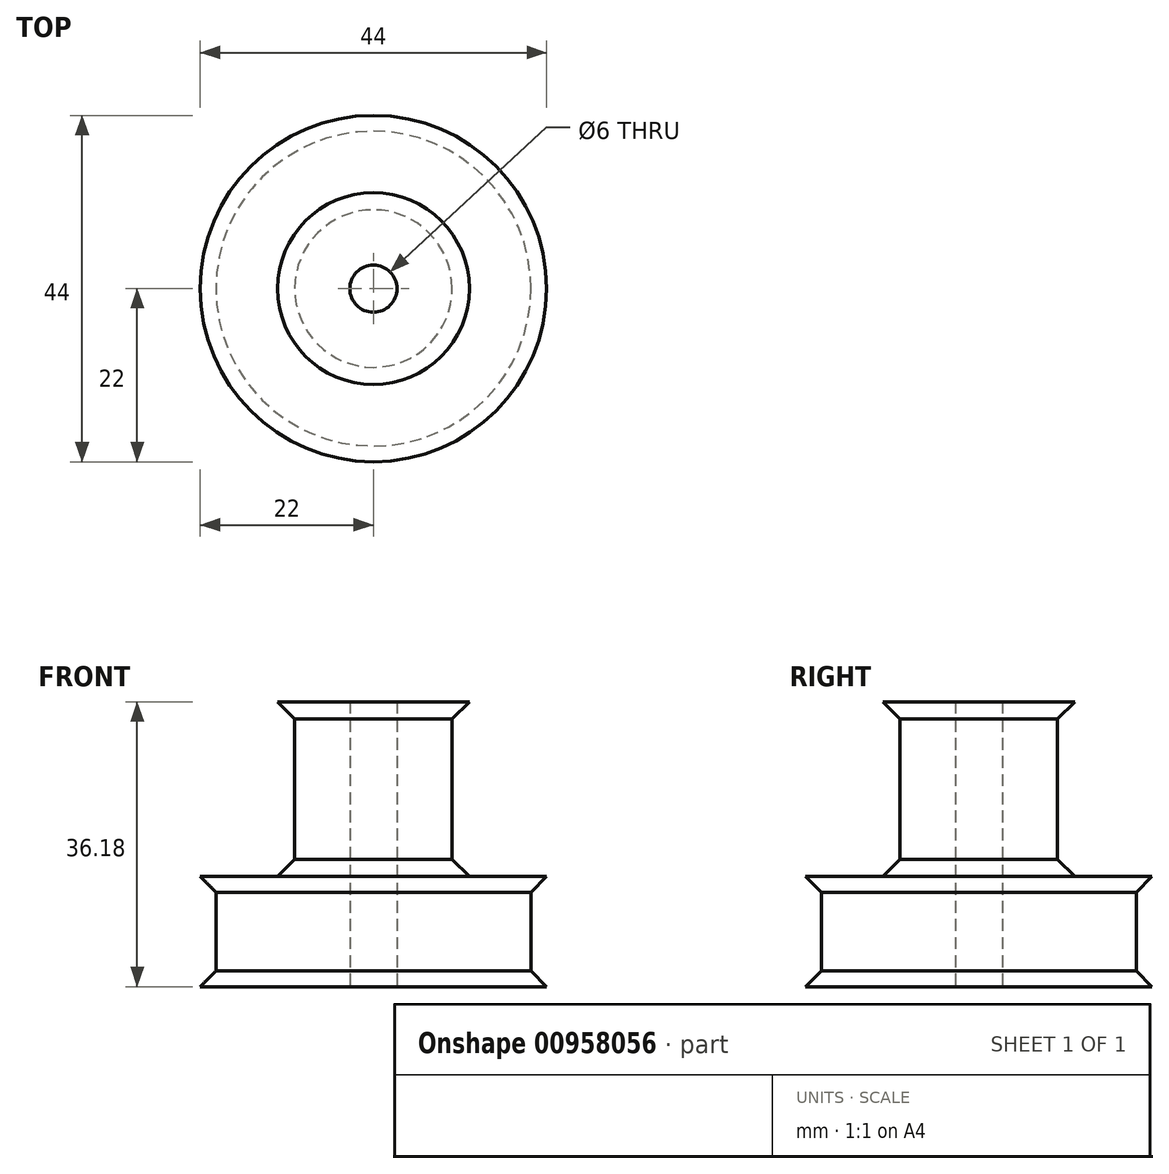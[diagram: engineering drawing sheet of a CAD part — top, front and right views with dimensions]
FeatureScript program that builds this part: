
annotation { "Feature Type Name" : "Feature", "Feature Type Description" : "" }
export const myFeature = defineFeature(function(context is Context, id is Id, definition is map)
    precondition{}
    {
        {
            var Q0;
            Q0=qCreatedBy(makeId("Front.planeOp"),FACE);
            var sketch = newSketch(context, id + "F0", { "sketchPlane" : qUnion([Q0])});
            skLineSegment(sketch, "E0", {"start": v(12.18, 36.18) * mm, "end": v(10, 34) * mm});
            skLineSegment(sketch, "E1", {"start": v(10, 34) * mm, "end": v(10, 16.18) * mm});
            skLineSegment(sketch, "E2", {"start": v(12.18, 14) * mm, "end": v(22, 14) * mm});
            skLineSegment(sketch, "E3", {"start": v(22, 14) * mm, "end": v(20, 12) * mm});
            skLineSegment(sketch, "E4", {"start": v(20, 12) * mm, "end": v(20, 2) * mm});
            skLineSegment(sketch, "E5", {"start": v(20, 2) * mm, "end": v(22, 0) * mm});
            skLineSegment(sketch, "E6", {"start": v(22, 0) * mm, "end": v(0, 0) * mm});
            skLineSegment(sketch, "E7", {"start": v(0, 0) * mm, "end": v(0, 36.18) * mm});
            skLineSegment(sketch, "E8", {"start": v(12.18, 36.18) * mm, "end": v(0, 36.18) * mm});
            skLineSegment(sketch, "E9", {"start": v(3, 36.18) * mm, "end": v(3, 0) * mm});
            skLineSegment(sketch, "E10", {"start": v(10, 16.18) * mm, "end": v(12.18, 14) * mm});
            skSolve(sketch);
        }
        {
            var Q0;
            {var subQ0=sQuery(id+"F0.wireOp",EDGE,"E0");Q0=makeQuery(id+"F0.imprint","IMPRINT",FACE,{"disambiguationData":[TD([[makeQuery(id+"F0.imprint","IMPRINT",EDGE,{"derivedFrom":subQ0}),-1.0]])]});}
            var Q1;
            Q1=sQuery(id+"F0.wireOp",EDGE,"E7");
            revolve(context, id + "F1", {"surfaceOperationType" : NewSurfaceOperationType.NEW, "entities" : qUnion([Q0]), "axis" : qUnion([Q1]), "revolveType" : RevolveType.FULL});
        }
    });
